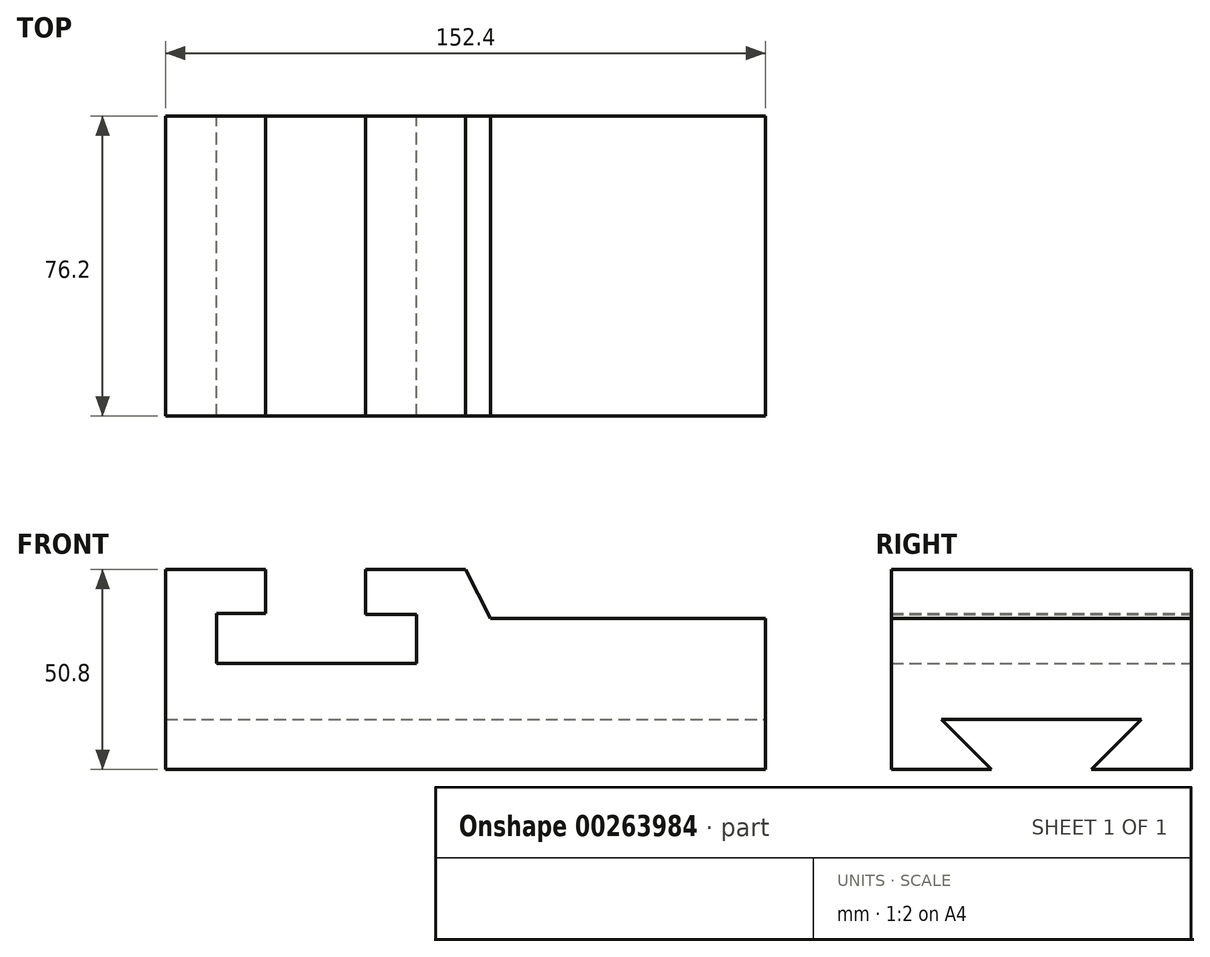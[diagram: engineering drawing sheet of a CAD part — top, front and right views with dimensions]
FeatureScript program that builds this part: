
annotation { "Feature Type Name" : "Feature", "Feature Type Description" : "" }
export const myFeature = defineFeature(function(context is Context, id is Id, definition is map)
    precondition{}
    {
        {
            var Q0;
            Q0=qCreatedBy(makeId("Front.planeOp"),FACE);
            var sketch = newSketch(context, id + "F0", { "sketchPlane" : qUnion([Q0])});
            skLineSegment(sketch, "E0", {"start": v(0, 0) * mm, "end": v(152.4, 0) * mm});
            skLineSegment(sketch, "E1", {"start": v(152.4, 0) * mm, "end": v(152.4, 38.36) * mm});
            skLineSegment(sketch, "E2", {"start": v(152.4, 38.36) * mm, "end": v(82.55, 38.36) * mm});
            skLineSegment(sketch, "E3", {"start": v(82.55, 38.36) * mm, "end": v(76.2, 50.8) * mm});
            skLineSegment(sketch, "E4", {"start": v(76.2, 50.8) * mm, "end": v(50.8, 50.8) * mm});
            skLineSegment(sketch, "E5", {"start": v(50.8, 50.8) * mm, "end": v(50.8, 39.4) * mm});
            skLineSegment(sketch, "E6", {"start": v(50.8, 39.4) * mm, "end": v(63.76, 39.4) * mm});
            skLineSegment(sketch, "E7", {"start": v(63.76, 39.4) * mm, "end": v(63.76, 26.96) * mm});
            skLineSegment(sketch, "E8", {"start": v(63.76, 26.96) * mm, "end": v(12.96, 26.96) * mm});
            skLineSegment(sketch, "E9", {"start": v(12.96, 26.96) * mm, "end": v(12.96, 39.66) * mm});
            skLineSegment(sketch, "E10", {"start": v(12.96, 39.66) * mm, "end": v(25.4, 39.66) * mm});
            skLineSegment(sketch, "E11", {"start": v(25.4, 39.66) * mm, "end": v(25.4, 50.8) * mm});
            skLineSegment(sketch, "E12", {"start": v(25.4, 50.8) * mm, "end": v(0, 50.8) * mm});
            skLineSegment(sketch, "E13", {"start": v(0, 50.8) * mm, "end": v(0, 0) * mm});
            skSolve(sketch);
        }
        {
            var Q0;
            Q0=makeQuery(id+"F0.imprint","IMPRINT",FACE,{"disambiguationData":[TD([[makeQuery(id+"F0.imprint","IMPRINT",EDGE,{"derivedFrom":sQuery(id+"F0.wireOp",EDGE,"E0")}),1.0]])]});
            extrude(context, id + "F1", {"entities" : qUnion([Q0]), "depth" : 76.2 * mm});
        }
        {
            var Q0;
            Q0=makeQuery(id+"F1.opExtrude","SWEPT_FACE",FACE,{"disambiguationData":[OSD([sQuery(id+"F0.wireOp",EDGE,"E1")])]});
            var sketch = newSketch(context, id + "F2", { "sketchPlane" : qUnion([Q0])});
            skLineSegment(sketch, "E14", {"start": v(-76.2, 0) * mm, "end": v(-50.8, 0) * mm});
            skLineSegment(sketch, "E15", {"start": v(-50.8, 0) * mm, "end": v(-63.5, 12.7) * mm});
            skLineSegment(sketch, "E16", {"start": v(-63.5, 12.7) * mm, "end": v(-12.7, 12.7) * mm});
            skLineSegment(sketch, "E17", {"start": v(-12.7, 12.7) * mm, "end": v(-25.4, 0) * mm});
            skLineSegment(sketch, "E18", {"start": v(-25.4, 0) * mm, "end": v(0, 0) * mm});
            skSolve(sketch);
        }
        {
            var Q0;
            Q0 = qSketchRegion(id + "F2", true);
            var Q1;
            {var subQ0=sQuery(id+"F2.wireOp",EDGE,"E15");Q1=makeQuery(id+"F2.imprint","IMPRINT",FACE,{"disambiguationData":[TD([[makeQuery(id+"F2.imprint","IMPRINT",EDGE,{"derivedFrom":subQ0}),-1.0]])]});}
            extrude(context, id + "F3", {"entities" : qUnion([Q0, Q1]), "operationType" : NewBodyOperationType.REMOVE, "oppositeDirection" : true, "depth" : 152.4 * mm});
        }
    });
